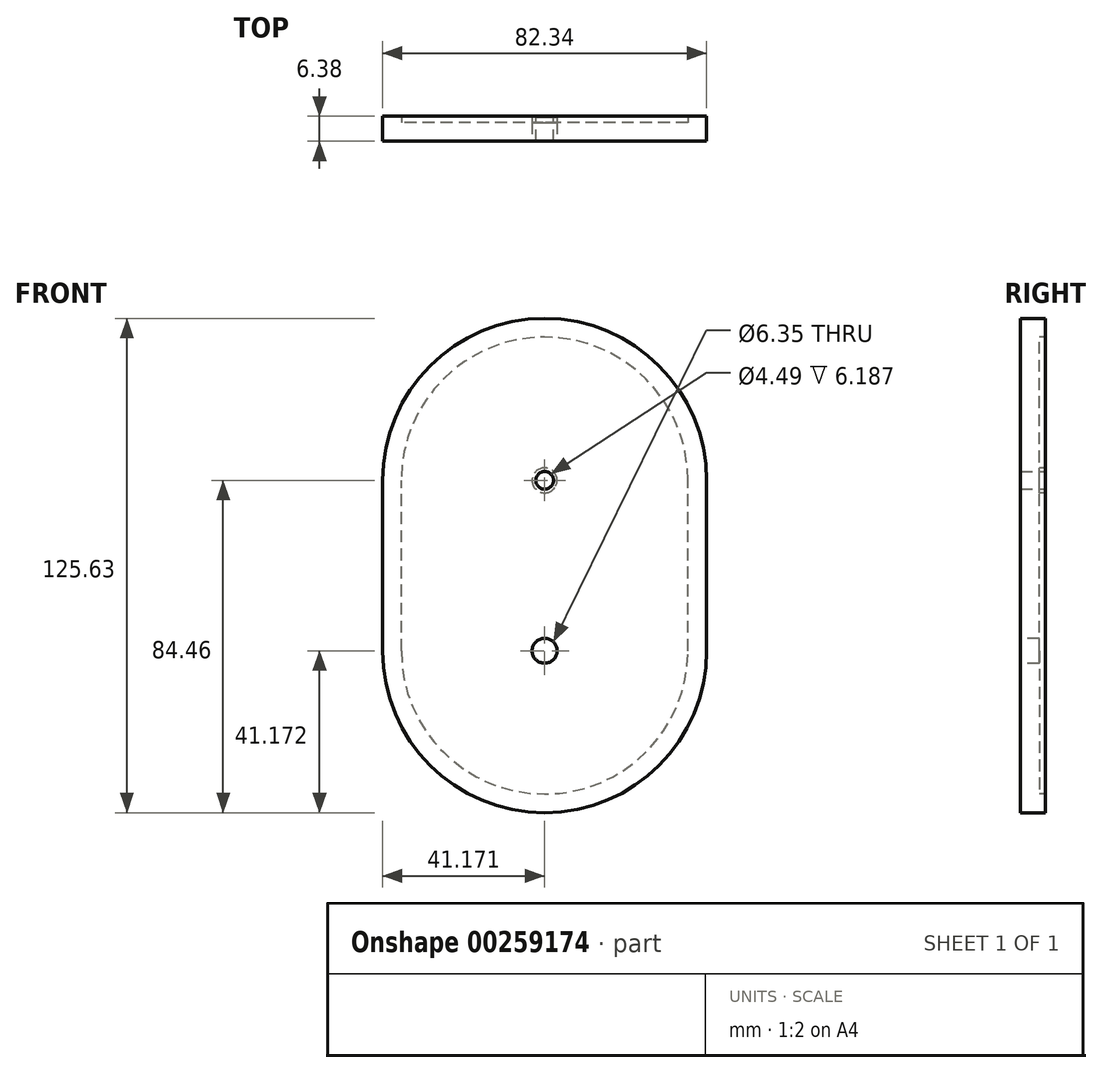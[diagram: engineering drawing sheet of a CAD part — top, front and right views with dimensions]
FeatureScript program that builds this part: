
annotation { "Feature Type Name" : "Feature", "Feature Type Description" : "" }
export const myFeature = defineFeature(function(context is Context, id is Id, definition is map)
    precondition{}
    {
        {
            var Q0;
            Q0=qCreatedBy(makeId("Front.planeOp"),FACE);
            var sketch = newSketch(context, id + "F0", { "sketchPlane" : qUnion([Q0])});
            skArc(sketch, "E0", {"start": v(82.34, 0) * mm, "mid": v(41.17, 41.17) * mm, "end": v(0, 0) * mm});
            skLineSegment(sketch, "E1", {"start": v(0, 0) * mm, "end": v(0, -43.29) * mm});
            skLineSegment(sketch, "E2", {"start": v(82.34, 0) * mm, "end": v(82.34, -43.29) * mm});
            skArc(sketch, "E3", {"start": v(0, -43.29) * mm, "mid": v(41.17, -84.46) * mm, "end": v(82.34, -43.29) * mm});
            skCircle(sketch, "E4", {"center": v(41.17, -43.29) * mm, "radius": 3.18 * mm});
            skSolve(sketch);
        }
        {
            var Q0;
            Q0 = qSketchRegion(id + "F0", true);
            extrude(context, id + "F1", {"entities" : qUnion([Q0]), "oppositeDirection" : true, "depth" : 4.76 * mm});
        }
        {
            var Q0;
            Q0=makeQuery(id+"F1.opExtrude","CAP_FACE",FACE,{"disambiguationData":[OSD([sQuery(id+"F0.wireOp",EDGE,"E0"),sQuery(id+"F0.wireOp",EDGE,"E1"),sQuery(id+"F0.wireOp",EDGE,"E2"),sQuery(id+"F0.wireOp",EDGE,"E3"),sQuery(id+"F0.wireOp",EDGE,"E4")])],"isStart":false});
            var sketch = newSketch(context, id + "F2", { "sketchPlane" : qUnion([Q0])});
            skArc(sketch, "E5", {"start": v(-77.58, -43.29) * mm, "mid": v(-41.17, -79.7) * mm, "end": v(-4.76, -43.29) * mm});
            skLineSegment(sketch, "E6", {"start": v(-77.58, -43.29) * mm, "end": v(-77.58, 0) * mm});
            skLineSegment(sketch, "E7", {"start": v(-4.76, -43.29) * mm, "end": v(-4.76, 0) * mm});
            skArc(sketch, "E8", {"start": v(-4.76, 0) * mm, "mid": v(-41.17, 36.4) * mm, "end": v(-77.58, 0) * mm});
            skArc(sketch, "E9", {"start": v(0, 0) * mm, "mid": v(-41.17, 41.17) * mm, "end": v(-82.34, 0) * mm});
            skArc(sketch, "E10", {"start": v(-82.34, -43.29) * mm, "mid": v(-41.17, -84.46) * mm, "end": v(0, -43.29) * mm});
            skLineSegment(sketch, "E11", {"start": v(-82.34, 0) * mm, "end": v(-82.34, -43.29) * mm});
            skLineSegment(sketch, "E12", {"start": v(0, 0) * mm, "end": v(0, -43.29) * mm});
            skSolve(sketch);
        }
        {
            var Q0;
            Q0 = qSketchRegion(id + "F2", true);
            extrude(context, id + "F3", {"entities" : qUnion([Q0]), "operationType" : NewBodyOperationType.ADD, "depth" : ((2 - (.2 + 3 / 16))) * mm});
        }
        {
            var Q0;
            Q0=makeQuery(id+"F1.opExtrude","CAP_FACE",FACE,{"disambiguationData":[OSD([sQuery(id+"F0.wireOp",EDGE,"E0"),sQuery(id+"F0.wireOp",EDGE,"E1"),sQuery(id+"F0.wireOp",EDGE,"E2"),sQuery(id+"F0.wireOp",EDGE,"E3"),sQuery(id+"F0.wireOp",EDGE,"E4")])],"isStart":false});
            var sketch = newSketch(context, id + "F4", { "sketchPlane" : qUnion([Q0])});
            skCircle(sketch, "E13", {"center": v(-41.17, 0) * mm, "radius": 3.17 * mm});
            skSolve(sketch);
        }
        {
            var Q0;
            Q0 = qSketchRegion(id + "F4", true);
            extrude(context, id + "F5", {"entities" : qUnion([Q0]), "operationType" : NewBodyOperationType.ADD, "depth" : ((2 - (.2 + 6 / 16))) * mm});
        }
        {
            var Q0;
            Q0=makeQuery(id+"F5.opExtrude","CAP_FACE",FACE,{"disambiguationData":[OSD([sQuery(id+"F4.wireOp",EDGE,"E13")])],"isStart":false});
            var sketch = newSketch(context, id + "F6", { "sketchPlane" : qUnion([Q0])});
            skLineSegment(sketch, "E14.bottom", {"start": v(-43.42, 2.25) * mm, "end": v(-38.93, 2.25) * mm, "construction": true});
            skLineSegment(sketch, "E14.top", {"start": v(-43.42, -2.25) * mm, "end": v(-38.93, -2.25) * mm, "construction": true});
            skLineSegment(sketch, "E14.left", {"start": v(-43.42, 2.25) * mm, "end": v(-43.42, -2.25) * mm, "construction": true});
            skLineSegment(sketch, "E14.right", {"start": v(-38.93, 2.25) * mm, "end": v(-38.93, -2.25) * mm, "construction": true});
            skCircle(sketch, "E15", {"center": v(-41.17, 0) * mm, "radius": 2.25 * mm});
            skSolve(sketch);
        }
        {
            var Q0;
            Q0 = qSketchRegion(id + "F6", true);
            extrude(context, id + "F7", {"entities" : qUnion([Q0]), "operationType" : NewBodyOperationType.REMOVE, "oppositeDirection" : true, "depth" : 12.7 * mm});
        }
    });
